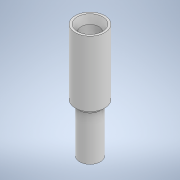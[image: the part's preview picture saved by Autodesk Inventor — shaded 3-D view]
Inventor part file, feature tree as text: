
AUTODESK INVENTOR PART (.ipt)
format: ipt  version: 2022 (Build 260153070, 153G)  size: 112,640 bytes
history: native  units: mm
features: revolve x1, sketch x1
ambient origin geometry x8: Origin, YZ Plane, XZ Plane, XY Plane, X Axis, Y Axis, Z Axis, Center Point
bodies: Solid1 (feature_tree)
feature tree (2):
  revolve  "Revolution1"  [1 undecoded]
  sketch  "Sketch1"  dims[d1=10.5mm d2=2.45mm d3=3.5mm d4=30.0deg d5=2.1mm d6=135.0deg d7=0.5mm d8=27.0mm d9=90.0deg]
note: 1 required parameter value undecoded (feature->parameter linkage not recoverable at this tier; creation-order binding heuristic only, values carry confidence <= 0.55)
